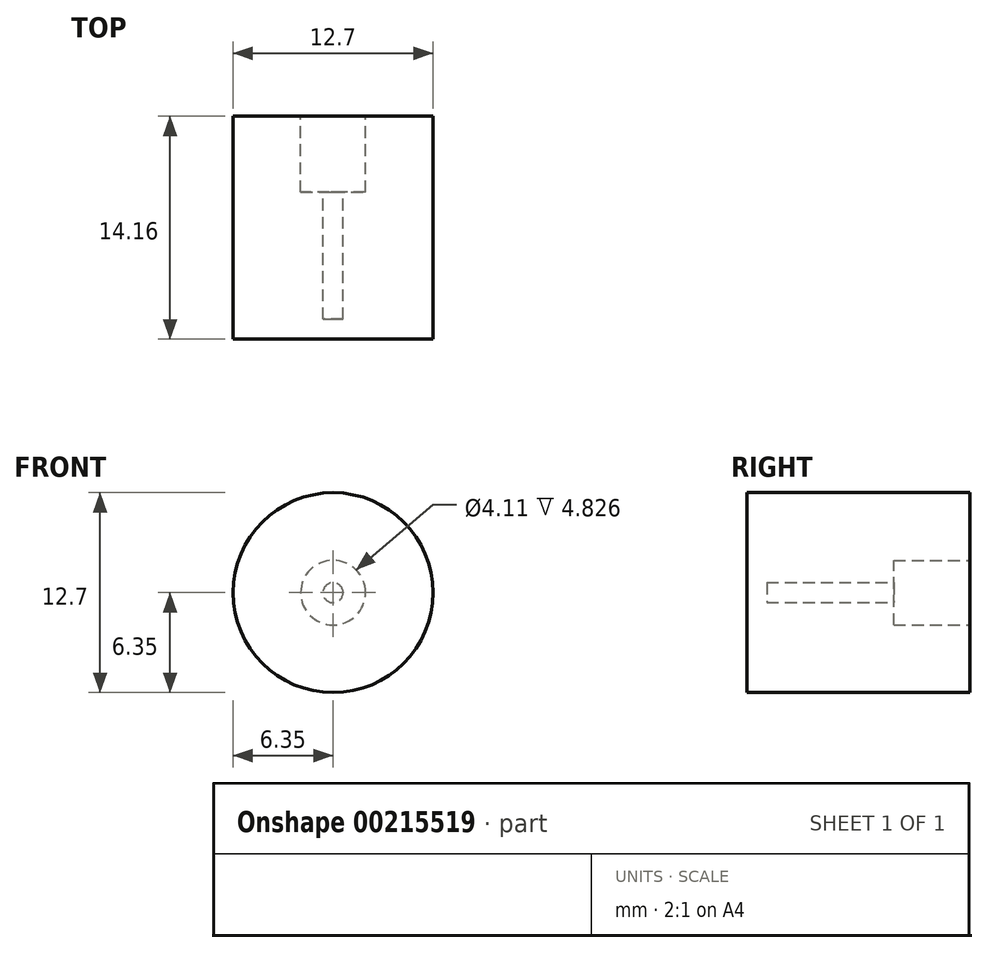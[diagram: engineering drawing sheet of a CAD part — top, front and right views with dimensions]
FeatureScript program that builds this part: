
annotation { "Feature Type Name" : "Feature", "Feature Type Description" : "" }
export const myFeature = defineFeature(function(context is Context, id is Id, definition is map)
    precondition{}
    {
        {
            var Q0;
            Q0=qCreatedBy(makeId("Front.planeOp"),FACE);
            var sketch = newSketch(context, id + "F0", { "sketchPlane" : qUnion([Q0])});
            skCircle(sketch, "E0", {"center": v(0, 0) * mm, "radius": 2.06 * mm});
            skCircle(sketch, "E1", {"center": v(0, 0) * mm, "radius": 6.35 * mm});
            skSolve(sketch);
        }
        {
            var Q0;
            Q0=makeQuery(id+"F0.imprint","IMPRINT",FACE,{"disambiguationData":[TD([[makeQuery(id+"F0.imprint","IMPRINT",EDGE,{"derivedFrom":sQuery(id+"F0.wireOp",EDGE,"E0")}),-1.0]])]});
            extrude(context, id + "F1", {"entities" : qUnion([Q0]), "depth" : 4.83 * mm});
        }
        {
            var Q0;
            Q0=makeQuery(id+"F1.opExtrude","CAP_FACE",FACE,{"disambiguationData":[OSD([sQuery(id+"F0.wireOp",EDGE,"E0"),sQuery(id+"F0.wireOp",EDGE,"E1")])],"isStart":false});
            var sketch = newSketch(context, id + "F2", { "sketchPlane" : qUnion([Q0])});
            skCircle(sketch, "E2", {"center": v(0, 0) * mm, "radius": 6.35 * mm});
            skSolve(sketch);
        }
        {
            var Q0;
            Q0 = qSketchRegion(id + "F2", true);
            extrude(context, id + "F3", {"entities" : qUnion([Q0]), "operationType" : NewBodyOperationType.ADD, "depth" : 9.33 * mm});
        }
        {
            var Q0;
            Q0=makeQuery(id+"F3.opExtrude","CAP_FACE",FACE,{"disambiguationData":[OSD([sQuery(id+"F2.wireOp",EDGE,"E2")])],"isStart":true});
            var sketch = newSketch(context, id + "F4", { "sketchPlane" : qUnion([Q0])});
            skCircle(sketch, "E3", {"center": v(0, 0) * mm, "radius": 0.64 * mm});
            skSolve(sketch);
        }
        {
            var Q0;
            Q0=makeQuery(id+"F4.imprint","IMPRINT",FACE,{"disambiguationData":[TD([[makeQuery(id+"F4.imprint","IMPRINT",EDGE,{"derivedFrom":sQuery(id+"F4.wireOp",EDGE,"E3")}),1.0]])]});
            extrude(context, id + "F5", {"entities" : qUnion([Q0]), "oppositeDirection" : true, "depth" : 8.06 * mm});
        }
    });
